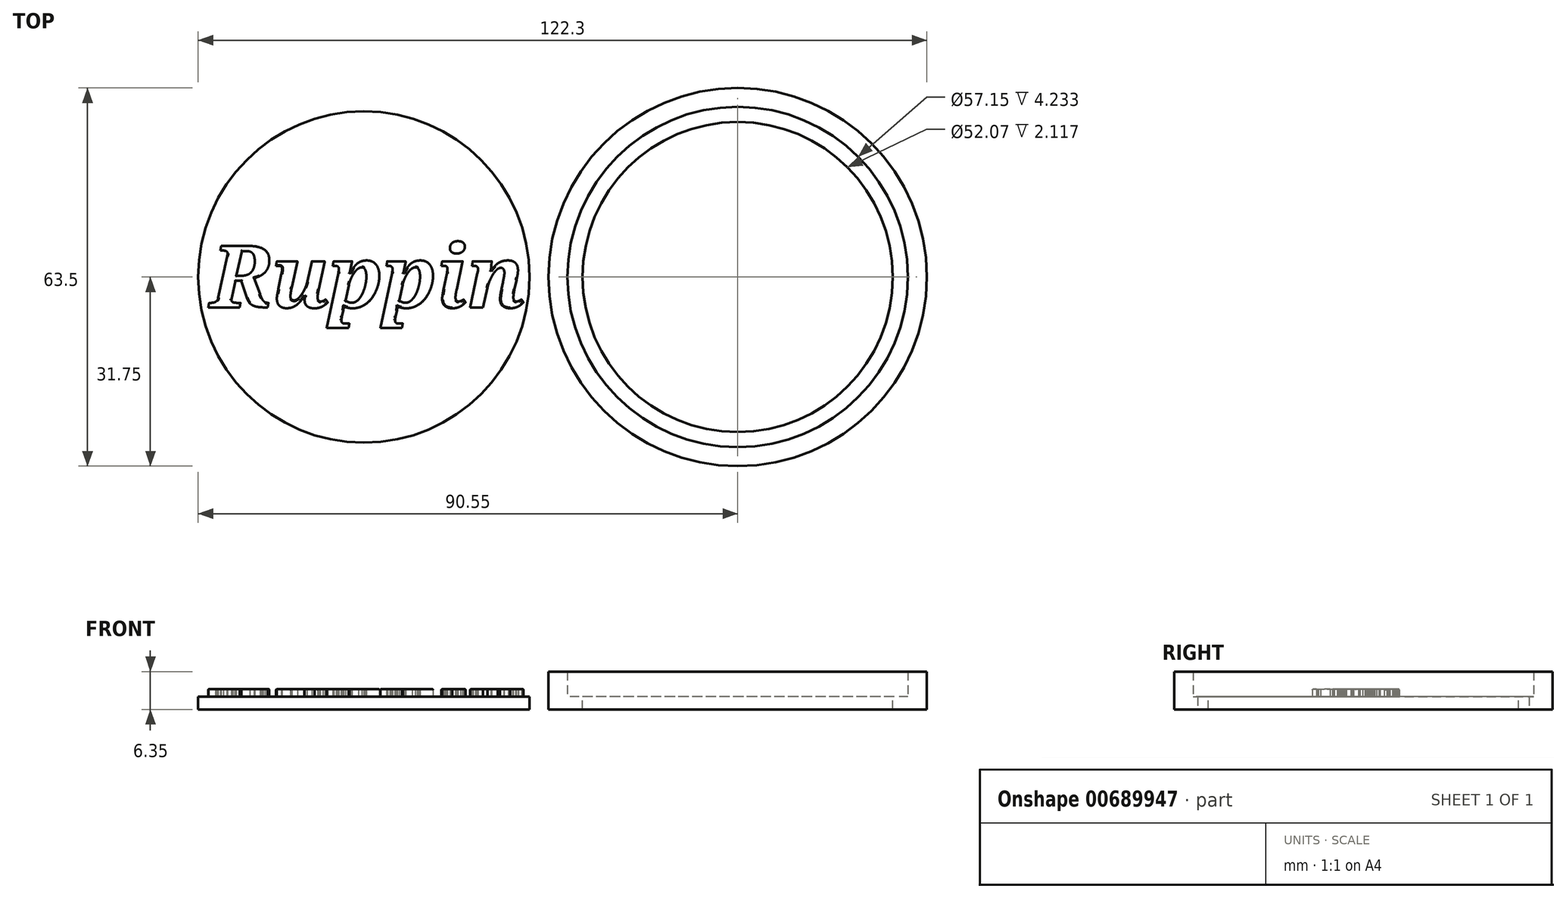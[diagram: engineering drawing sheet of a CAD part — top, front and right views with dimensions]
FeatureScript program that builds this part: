
annotation { "Feature Type Name" : "Feature", "Feature Type Description" : "" }
export const myFeature = defineFeature(function(context is Context, id is Id, definition is map)
    precondition{}
    {
        {
            var Q0;
            Q0=qCreatedBy(makeId("Top.planeOp"),FACE);
            var sketch = newSketch(context, id + "F0", { "sketchPlane" : qUnion([Q0])});
            skCircle(sketch, "E0", {"center": v(0, 0) * mm, "radius": 31.75 * mm});
            skCircle(sketch, "E1.0", {"center": v(0, 0) * mm, "radius": 28.57 * mm});
            skCircle(sketch, "E2.0", {"center": v(0, 0) * mm, "radius": 26.04 * mm});
            skCircle(sketch, "E3.0", {"center": v(0, 0) * mm, "radius": 27.81 * mm});
            skSolve(sketch);
        }
        {
            var Q0;
            Q0=makeQuery(id+"F0.imprint","IMPRINT",FACE,{"disambiguationData":[TD([[makeQuery(id+"F0.imprint","IMPRINT",EDGE,{"derivedFrom":sQuery(id+"F0.wireOp",EDGE,"E0")}),1.0]])]});
            extrude(context, id + "F1", {"entities" : qUnion([Q0]), "depth" : 2.12 * mm, "offsetDistance" : 25.4 * mm});
        }
        {
            var Q0;
            Q0=makeQuery(id+"F1.opExtrude","CAP_FACE",FACE,{"disambiguationData":[OSD([sQuery(id+"F0.wireOp",EDGE,"E0"),sQuery(id+"F0.wireOp",EDGE,"E1.0")])],"isStart":false});
            extrude(context, id + "F2", {"entities" : qUnion([Q0]), "operationType" : NewBodyOperationType.ADD, "depth" : 2.12 * mm, "offsetDistance" : 25.4 * mm});
        }
        {
            var Q0;
            Q0=makeQuery(id+"F0.imprint","IMPRINT",FACE,{"disambiguationData":[TD([[makeQuery(id+"F0.imprint","IMPRINT",EDGE,{"derivedFrom":sQuery(id+"F0.wireOp",EDGE,"E1.0")}),1.0]])]});
            var Q1;
            Q1=makeQuery(id+"F0.imprint","IMPRINT",FACE,{"disambiguationData":[TD([[makeQuery(id+"F0.imprint","IMPRINT",EDGE,{"derivedFrom":sQuery(id+"F0.wireOp",EDGE,"E0")}),1.0]])]});
            var Q2;
            Q2=makeQuery(id+"F0.imprint","IMPRINT",FACE,{"disambiguationData":[TD([[makeQuery(id+"F0.imprint","IMPRINT",EDGE,{"derivedFrom":sQuery(id+"F0.wireOp",EDGE,"E2.0")}),-1.0]])]});
            extrude(context, id + "F3", {"entities" : qUnion([Q0, Q1, Q2]), "operationType" : NewBodyOperationType.ADD, "oppositeDirection" : true, "depth" : 2.12 * mm, "offsetDistance" : 25.4 * mm});
        }
        {
            var Q0;
            Q0=makeQuery(id+"F0.imprint","IMPRINT",FACE,{"disambiguationData":[TD([[makeQuery(id+"F0.imprint","IMPRINT",EDGE,{"derivedFrom":sQuery(id+"F0.wireOp",EDGE,"E2.0")}),1.0]])]});
            var Q1;
            Q1=makeQuery(id+"F0.imprint","IMPRINT",FACE,{"disambiguationData":[TD([[makeQuery(id+"F0.imprint","IMPRINT",EDGE,{"derivedFrom":sQuery(id+"F0.wireOp",EDGE,"E2.0")}),-1.0]])]});
            extrude(context, id + "F4", {"entities" : qUnion([Q0, Q1]), "depth" : 2.12 * mm, "offsetDistance" : 25.4 * mm});
        }
        {
            var Q0;
            Q0=makeQuery(id+"F4.opExtrude","CAP_FACE",FACE,{"disambiguationData":[OSD([sQuery(id+"F0.wireOp",EDGE,"E3.0")])],"isStart":false});
            var sketch = newSketch(context, id + "F5", { "sketchPlane" : qUnion([Q0])});
            skText(sketch, "E4", { "text": "Ruppin", "fontName": "NotoSerif-BoldItalic.ttf"});
            const initialGuessF5  = {"E4": [-0.02578, -0.00511, 1, 0, 0.01041]};
            skSetInitialGuess(sketch, initialGuessF5);
            skSolve(sketch);
        }
        {
            var Q0;
            Q0 = qSketchRegion(id + "F5", true);
            extrude(context, id + "F6", {"entities" : qUnion([Q0]), "operationType" : NewBodyOperationType.ADD, "depth" : 1.27 * mm, "offsetDistance" : 25.4 * mm});
        }
        {
            var Q0;
            Q0=makeQuery(id+"F6.opExtrude","CAP_FACE",FACE,{"disambiguationData":[OSD([sQuery(id+"F5.wireOp",EDGE,"E4.sketch_text.stroke-0"),sQuery(id+"F5.wireOp",EDGE,"E4.sketch_text.stroke-1"),sQuery(id+"F5.wireOp",EDGE,"E4.sketch_text.stroke-2"),sQuery(id+"F5.wireOp",EDGE,"E4.sketch_text.stroke-3"),sQuery(id+"F5.wireOp",EDGE,"E4.sketch_text.stroke-4"),sQuery(id+"F5.wireOp",EDGE,"E4.sketch_text.stroke-5"),sQuery(id+"F5.wireOp",EDGE,"E4.sketch_text.stroke-6"),sQuery(id+"F5.wireOp",EDGE,"E4.sketch_text.stroke-7"),sQuery(id+"F5.wireOp",EDGE,"E4.sketch_text.stroke-8"),sQuery(id+"F5.wireOp",EDGE,"E4.sketch_text.stroke-9"),sQuery(id+"F5.wireOp",EDGE,"E4.sketch_text.stroke-10"),sQuery(id+"F5.wireOp",EDGE,"E4.sketch_text.stroke-11"),sQuery(id+"F5.wireOp",EDGE,"E4.sketch_text.stroke-12"),sQuery(id+"F5.wireOp",EDGE,"E4.sketch_text.stroke-13"),sQuery(id+"F5.wireOp",EDGE,"E4.sketch_text.stroke-14"),sQuery(id+"F5.wireOp",EDGE,"E4.sketch_text.stroke-15"),sQuery(id+"F5.wireOp",EDGE,"E4.sketch_text.stroke-16"),sQuery(id+"F5.wireOp",EDGE,"E4.sketch_text.stroke-17"),sQuery(id+"F5.wireOp",EDGE,"E4.sketch_text.stroke-18"),sQuery(id+"F5.wireOp",EDGE,"E4.sketch_text.stroke-19"),sQuery(id+"F5.wireOp",EDGE,"E4.sketch_text.stroke-20"),sQuery(id+"F5.wireOp",EDGE,"E4.sketch_text.stroke-21"),sQuery(id+"F5.wireOp",EDGE,"E4.sketch_text.stroke-22"),sQuery(id+"F5.wireOp",EDGE,"E4.sketch_text.stroke-23"),sQuery(id+"F5.wireOp",EDGE,"E4.sketch_text.stroke-24"),sQuery(id+"F5.wireOp",EDGE,"E4.sketch_text.stroke-25"),sQuery(id+"F5.wireOp",EDGE,"E4.sketch_text.stroke-26"),sQuery(id+"F5.wireOp",EDGE,"E4.sketch_text.stroke-27"),sQuery(id+"F5.wireOp",EDGE,"E4.sketch_text.stroke-28"),sQuery(id+"F5.wireOp",EDGE,"E4.sketch_text.stroke-29"),sQuery(id+"F5.wireOp",EDGE,"E4.sketch_text.stroke-30"),sQuery(id+"F5.wireOp",EDGE,"E4.sketch_text.stroke-31"),sQuery(id+"F5.wireOp",EDGE,"E4.sketch_text.stroke-32"),sQuery(id+"F5.wireOp",EDGE,"E4.sketch_text.stroke-33"),sQuery(id+"F5.wireOp",EDGE,"E4.sketch_text.stroke-34"),sQuery(id+"F5.wireOp",EDGE,"E4.sketch_text.stroke-35"),sQuery(id+"F5.wireOp",EDGE,"E4.sketch_text.stroke-36"),sQuery(id+"F5.wireOp",EDGE,"E4.sketch_text.stroke-37"),sQuery(id+"F5.wireOp",EDGE,"E4.sketch_text.stroke-38"),sQuery(id+"F5.wireOp",EDGE,"E4.sketch_text.stroke-39"),sQuery(id+"F5.wireOp",EDGE,"E4.sketch_text.stroke-40"),sQuery(id+"F5.wireOp",EDGE,"E4.sketch_text.stroke-41"),sQuery(id+"F5.wireOp",EDGE,"E4.sketch_text.stroke-42"),sQuery(id+"F5.wireOp",EDGE,"E4.sketch_text.stroke-43"),sQuery(id+"F5.wireOp",EDGE,"E4.sketch_text.stroke-44"),sQuery(id+"F5.wireOp",EDGE,"E4.sketch_text.stroke-45"),sQuery(id+"F5.wireOp",EDGE,"E4.sketch_text.stroke-46"),sQuery(id+"F5.wireOp",EDGE,"E4.sketch_text.stroke-47"),sQuery(id+"F5.wireOp",EDGE,"E4.sketch_text.stroke-48"),sQuery(id+"F5.wireOp",EDGE,"E4.sketch_text.stroke-49"),sQuery(id+"F5.wireOp",EDGE,"E4.sketch_text.stroke-50"),sQuery(id+"F5.wireOp",EDGE,"E4.sketch_text.stroke-51"),sQuery(id+"F5.wireOp",EDGE,"E4.sketch_text.stroke-52"),sQuery(id+"F5.wireOp",EDGE,"E4.sketch_text.stroke-53"),sQuery(id+"F5.wireOp",EDGE,"E4.sketch_text.stroke-54"),sQuery(id+"F5.wireOp",EDGE,"E4.sketch_text.stroke-55")])],"isStart":false});
            var Q1;
            Q1=makeQuery(id+"F6.opExtrude","CAP_FACE",FACE,{"disambiguationData":[OSD([sQuery(id+"F5.wireOp",EDGE,"E4.sketch_text.stroke-56"),sQuery(id+"F5.wireOp",EDGE,"E4.sketch_text.stroke-57"),sQuery(id+"F5.wireOp",EDGE,"E4.sketch_text.stroke-58"),sQuery(id+"F5.wireOp",EDGE,"E4.sketch_text.stroke-59"),sQuery(id+"F5.wireOp",EDGE,"E4.sketch_text.stroke-60"),sQuery(id+"F5.wireOp",EDGE,"E4.sketch_text.stroke-61"),sQuery(id+"F5.wireOp",EDGE,"E4.sketch_text.stroke-62"),sQuery(id+"F5.wireOp",EDGE,"E4.sketch_text.stroke-63"),sQuery(id+"F5.wireOp",EDGE,"E4.sketch_text.stroke-64"),sQuery(id+"F5.wireOp",EDGE,"E4.sketch_text.stroke-65"),sQuery(id+"F5.wireOp",EDGE,"E4.sketch_text.stroke-66"),sQuery(id+"F5.wireOp",EDGE,"E4.sketch_text.stroke-67"),sQuery(id+"F5.wireOp",EDGE,"E4.sketch_text.stroke-68"),sQuery(id+"F5.wireOp",EDGE,"E4.sketch_text.stroke-69"),sQuery(id+"F5.wireOp",EDGE,"E4.sketch_text.stroke-70"),sQuery(id+"F5.wireOp",EDGE,"E4.sketch_text.stroke-71"),sQuery(id+"F5.wireOp",EDGE,"E4.sketch_text.stroke-72"),sQuery(id+"F5.wireOp",EDGE,"E4.sketch_text.stroke-73"),sQuery(id+"F5.wireOp",EDGE,"E4.sketch_text.stroke-74"),sQuery(id+"F5.wireOp",EDGE,"E4.sketch_text.stroke-75"),sQuery(id+"F5.wireOp",EDGE,"E4.sketch_text.stroke-76"),sQuery(id+"F5.wireOp",EDGE,"E4.sketch_text.stroke-77"),sQuery(id+"F5.wireOp",EDGE,"E4.sketch_text.stroke-78"),sQuery(id+"F5.wireOp",EDGE,"E4.sketch_text.stroke-79"),sQuery(id+"F5.wireOp",EDGE,"E4.sketch_text.stroke-80"),sQuery(id+"F5.wireOp",EDGE,"E4.sketch_text.stroke-81"),sQuery(id+"F5.wireOp",EDGE,"E4.sketch_text.stroke-82"),sQuery(id+"F5.wireOp",EDGE,"E4.sketch_text.stroke-83"),sQuery(id+"F5.wireOp",EDGE,"E4.sketch_text.stroke-84"),sQuery(id+"F5.wireOp",EDGE,"E4.sketch_text.stroke-85"),sQuery(id+"F5.wireOp",EDGE,"E4.sketch_text.stroke-86"),sQuery(id+"F5.wireOp",EDGE,"E4.sketch_text.stroke-87"),sQuery(id+"F5.wireOp",EDGE,"E4.sketch_text.stroke-88"),sQuery(id+"F5.wireOp",EDGE,"E4.sketch_text.stroke-89"),sQuery(id+"F5.wireOp",EDGE,"E4.sketch_text.stroke-90"),sQuery(id+"F5.wireOp",EDGE,"E4.sketch_text.stroke-91"),sQuery(id+"F5.wireOp",EDGE,"E4.sketch_text.stroke-92"),sQuery(id+"F5.wireOp",EDGE,"E4.sketch_text.stroke-93"),sQuery(id+"F5.wireOp",EDGE,"E4.sketch_text.stroke-94"),sQuery(id+"F5.wireOp",EDGE,"E4.sketch_text.stroke-95"),sQuery(id+"F5.wireOp",EDGE,"E4.sketch_text.stroke-96"),sQuery(id+"F5.wireOp",EDGE,"E4.sketch_text.stroke-97"),sQuery(id+"F5.wireOp",EDGE,"E4.sketch_text.stroke-98"),sQuery(id+"F5.wireOp",EDGE,"E4.sketch_text.stroke-99"),sQuery(id+"F5.wireOp",EDGE,"E4.sketch_text.stroke-100"),sQuery(id+"F5.wireOp",EDGE,"E4.sketch_text.stroke-101"),sQuery(id+"F5.wireOp",EDGE,"E4.sketch_text.stroke-102"),sQuery(id+"F5.wireOp",EDGE,"E4.sketch_text.stroke-103"),sQuery(id+"F5.wireOp",EDGE,"E4.sketch_text.stroke-104"),sQuery(id+"F5.wireOp",EDGE,"E4.sketch_text.stroke-105"),sQuery(id+"F5.wireOp",EDGE,"E4.sketch_text.stroke-106"),sQuery(id+"F5.wireOp",EDGE,"E4.sketch_text.stroke-107")])],"isStart":false});
            var Q2;
            Q2=makeQuery(id+"F6.opExtrude","CAP_FACE",FACE,{"disambiguationData":[OSD([sQuery(id+"F5.wireOp",EDGE,"E4.sketch_text.stroke-108"),sQuery(id+"F5.wireOp",EDGE,"E4.sketch_text.stroke-109"),sQuery(id+"F5.wireOp",EDGE,"E4.sketch_text.stroke-110"),sQuery(id+"F5.wireOp",EDGE,"E4.sketch_text.stroke-111"),sQuery(id+"F5.wireOp",EDGE,"E4.sketch_text.stroke-112"),sQuery(id+"F5.wireOp",EDGE,"E4.sketch_text.stroke-113"),sQuery(id+"F5.wireOp",EDGE,"E4.sketch_text.stroke-114"),sQuery(id+"F5.wireOp",EDGE,"E4.sketch_text.stroke-115"),sQuery(id+"F5.wireOp",EDGE,"E4.sketch_text.stroke-116"),sQuery(id+"F5.wireOp",EDGE,"E4.sketch_text.stroke-117"),sQuery(id+"F5.wireOp",EDGE,"E4.sketch_text.stroke-118"),sQuery(id+"F5.wireOp",EDGE,"E4.sketch_text.stroke-119"),sQuery(id+"F5.wireOp",EDGE,"E4.sketch_text.stroke-120"),sQuery(id+"F5.wireOp",EDGE,"E4.sketch_text.stroke-121"),sQuery(id+"F5.wireOp",EDGE,"E4.sketch_text.stroke-122"),sQuery(id+"F5.wireOp",EDGE,"E4.sketch_text.stroke-123"),sQuery(id+"F5.wireOp",EDGE,"E4.sketch_text.stroke-124"),sQuery(id+"F5.wireOp",EDGE,"E4.sketch_text.stroke-125"),sQuery(id+"F5.wireOp",EDGE,"E4.sketch_text.stroke-126"),sQuery(id+"F5.wireOp",EDGE,"E4.sketch_text.stroke-127"),sQuery(id+"F5.wireOp",EDGE,"E4.sketch_text.stroke-128"),sQuery(id+"F5.wireOp",EDGE,"E4.sketch_text.stroke-129"),sQuery(id+"F5.wireOp",EDGE,"E4.sketch_text.stroke-130"),sQuery(id+"F5.wireOp",EDGE,"E4.sketch_text.stroke-131"),sQuery(id+"F5.wireOp",EDGE,"E4.sketch_text.stroke-132"),sQuery(id+"F5.wireOp",EDGE,"E4.sketch_text.stroke-133"),sQuery(id+"F5.wireOp",EDGE,"E4.sketch_text.stroke-134"),sQuery(id+"F5.wireOp",EDGE,"E4.sketch_text.stroke-135"),sQuery(id+"F5.wireOp",EDGE,"E4.sketch_text.stroke-136"),sQuery(id+"F5.wireOp",EDGE,"E4.sketch_text.stroke-137"),sQuery(id+"F5.wireOp",EDGE,"E4.sketch_text.stroke-138"),sQuery(id+"F5.wireOp",EDGE,"E4.sketch_text.stroke-139"),sQuery(id+"F5.wireOp",EDGE,"E4.sketch_text.stroke-140"),sQuery(id+"F5.wireOp",EDGE,"E4.sketch_text.stroke-141"),sQuery(id+"F5.wireOp",EDGE,"E4.sketch_text.stroke-142"),sQuery(id+"F5.wireOp",EDGE,"E4.sketch_text.stroke-143"),sQuery(id+"F5.wireOp",EDGE,"E4.sketch_text.stroke-144"),sQuery(id+"F5.wireOp",EDGE,"E4.sketch_text.stroke-145"),sQuery(id+"F5.wireOp",EDGE,"E4.sketch_text.stroke-146"),sQuery(id+"F5.wireOp",EDGE,"E4.sketch_text.stroke-147"),sQuery(id+"F5.wireOp",EDGE,"E4.sketch_text.stroke-148"),sQuery(id+"F5.wireOp",EDGE,"E4.sketch_text.stroke-149"),sQuery(id+"F5.wireOp",EDGE,"E4.sketch_text.stroke-150"),sQuery(id+"F5.wireOp",EDGE,"E4.sketch_text.stroke-151"),sQuery(id+"F5.wireOp",EDGE,"E4.sketch_text.stroke-152"),sQuery(id+"F5.wireOp",EDGE,"E4.sketch_text.stroke-153"),sQuery(id+"F5.wireOp",EDGE,"E4.sketch_text.stroke-154"),sQuery(id+"F5.wireOp",EDGE,"E4.sketch_text.stroke-155"),sQuery(id+"F5.wireOp",EDGE,"E4.sketch_text.stroke-156"),sQuery(id+"F5.wireOp",EDGE,"E4.sketch_text.stroke-157"),sQuery(id+"F5.wireOp",EDGE,"E4.sketch_text.stroke-158"),sQuery(id+"F5.wireOp",EDGE,"E4.sketch_text.stroke-159"),sQuery(id+"F5.wireOp",EDGE,"E4.sketch_text.stroke-160"),sQuery(id+"F5.wireOp",EDGE,"E4.sketch_text.stroke-161"),sQuery(id+"F5.wireOp",EDGE,"E4.sketch_text.stroke-162"),sQuery(id+"F5.wireOp",EDGE,"E4.sketch_text.stroke-163"),sQuery(id+"F5.wireOp",EDGE,"E4.sketch_text.stroke-164"),sQuery(id+"F5.wireOp",EDGE,"E4.sketch_text.stroke-165"),sQuery(id+"F5.wireOp",EDGE,"E4.sketch_text.stroke-166"),sQuery(id+"F5.wireOp",EDGE,"E4.sketch_text.stroke-167"),sQuery(id+"F5.wireOp",EDGE,"E4.sketch_text.stroke-168"),sQuery(id+"F5.wireOp",EDGE,"E4.sketch_text.stroke-169"),sQuery(id+"F5.wireOp",EDGE,"E4.sketch_text.stroke-170"),sQuery(id+"F5.wireOp",EDGE,"E4.sketch_text.stroke-171"),sQuery(id+"F5.wireOp",EDGE,"E4.sketch_text.stroke-172"),sQuery(id+"F5.wireOp",EDGE,"E4.sketch_text.stroke-173")])],"isStart":false});
            var Q3;
            Q3=makeQuery(id+"F6.opExtrude","CAP_FACE",FACE,{"disambiguationData":[OSD([sQuery(id+"F5.wireOp",EDGE,"E4.sketch_text.stroke-174"),sQuery(id+"F5.wireOp",EDGE,"E4.sketch_text.stroke-175"),sQuery(id+"F5.wireOp",EDGE,"E4.sketch_text.stroke-176"),sQuery(id+"F5.wireOp",EDGE,"E4.sketch_text.stroke-177"),sQuery(id+"F5.wireOp",EDGE,"E4.sketch_text.stroke-178"),sQuery(id+"F5.wireOp",EDGE,"E4.sketch_text.stroke-179"),sQuery(id+"F5.wireOp",EDGE,"E4.sketch_text.stroke-180"),sQuery(id+"F5.wireOp",EDGE,"E4.sketch_text.stroke-181"),sQuery(id+"F5.wireOp",EDGE,"E4.sketch_text.stroke-182"),sQuery(id+"F5.wireOp",EDGE,"E4.sketch_text.stroke-183"),sQuery(id+"F5.wireOp",EDGE,"E4.sketch_text.stroke-184"),sQuery(id+"F5.wireOp",EDGE,"E4.sketch_text.stroke-185"),sQuery(id+"F5.wireOp",EDGE,"E4.sketch_text.stroke-186"),sQuery(id+"F5.wireOp",EDGE,"E4.sketch_text.stroke-187"),sQuery(id+"F5.wireOp",EDGE,"E4.sketch_text.stroke-188"),sQuery(id+"F5.wireOp",EDGE,"E4.sketch_text.stroke-189"),sQuery(id+"F5.wireOp",EDGE,"E4.sketch_text.stroke-190"),sQuery(id+"F5.wireOp",EDGE,"E4.sketch_text.stroke-191"),sQuery(id+"F5.wireOp",EDGE,"E4.sketch_text.stroke-192"),sQuery(id+"F5.wireOp",EDGE,"E4.sketch_text.stroke-193"),sQuery(id+"F5.wireOp",EDGE,"E4.sketch_text.stroke-194"),sQuery(id+"F5.wireOp",EDGE,"E4.sketch_text.stroke-195"),sQuery(id+"F5.wireOp",EDGE,"E4.sketch_text.stroke-196"),sQuery(id+"F5.wireOp",EDGE,"E4.sketch_text.stroke-197"),sQuery(id+"F5.wireOp",EDGE,"E4.sketch_text.stroke-198"),sQuery(id+"F5.wireOp",EDGE,"E4.sketch_text.stroke-199"),sQuery(id+"F5.wireOp",EDGE,"E4.sketch_text.stroke-200"),sQuery(id+"F5.wireOp",EDGE,"E4.sketch_text.stroke-201"),sQuery(id+"F5.wireOp",EDGE,"E4.sketch_text.stroke-202"),sQuery(id+"F5.wireOp",EDGE,"E4.sketch_text.stroke-203"),sQuery(id+"F5.wireOp",EDGE,"E4.sketch_text.stroke-204"),sQuery(id+"F5.wireOp",EDGE,"E4.sketch_text.stroke-205"),sQuery(id+"F5.wireOp",EDGE,"E4.sketch_text.stroke-206"),sQuery(id+"F5.wireOp",EDGE,"E4.sketch_text.stroke-207"),sQuery(id+"F5.wireOp",EDGE,"E4.sketch_text.stroke-208"),sQuery(id+"F5.wireOp",EDGE,"E4.sketch_text.stroke-209"),sQuery(id+"F5.wireOp",EDGE,"E4.sketch_text.stroke-210"),sQuery(id+"F5.wireOp",EDGE,"E4.sketch_text.stroke-211"),sQuery(id+"F5.wireOp",EDGE,"E4.sketch_text.stroke-212"),sQuery(id+"F5.wireOp",EDGE,"E4.sketch_text.stroke-213"),sQuery(id+"F5.wireOp",EDGE,"E4.sketch_text.stroke-214"),sQuery(id+"F5.wireOp",EDGE,"E4.sketch_text.stroke-215"),sQuery(id+"F5.wireOp",EDGE,"E4.sketch_text.stroke-216"),sQuery(id+"F5.wireOp",EDGE,"E4.sketch_text.stroke-217"),sQuery(id+"F5.wireOp",EDGE,"E4.sketch_text.stroke-218"),sQuery(id+"F5.wireOp",EDGE,"E4.sketch_text.stroke-219"),sQuery(id+"F5.wireOp",EDGE,"E4.sketch_text.stroke-220"),sQuery(id+"F5.wireOp",EDGE,"E4.sketch_text.stroke-221"),sQuery(id+"F5.wireOp",EDGE,"E4.sketch_text.stroke-222"),sQuery(id+"F5.wireOp",EDGE,"E4.sketch_text.stroke-223"),sQuery(id+"F5.wireOp",EDGE,"E4.sketch_text.stroke-224"),sQuery(id+"F5.wireOp",EDGE,"E4.sketch_text.stroke-225"),sQuery(id+"F5.wireOp",EDGE,"E4.sketch_text.stroke-226"),sQuery(id+"F5.wireOp",EDGE,"E4.sketch_text.stroke-227"),sQuery(id+"F5.wireOp",EDGE,"E4.sketch_text.stroke-228"),sQuery(id+"F5.wireOp",EDGE,"E4.sketch_text.stroke-229"),sQuery(id+"F5.wireOp",EDGE,"E4.sketch_text.stroke-230"),sQuery(id+"F5.wireOp",EDGE,"E4.sketch_text.stroke-231"),sQuery(id+"F5.wireOp",EDGE,"E4.sketch_text.stroke-232"),sQuery(id+"F5.wireOp",EDGE,"E4.sketch_text.stroke-233"),sQuery(id+"F5.wireOp",EDGE,"E4.sketch_text.stroke-234"),sQuery(id+"F5.wireOp",EDGE,"E4.sketch_text.stroke-235"),sQuery(id+"F5.wireOp",EDGE,"E4.sketch_text.stroke-236"),sQuery(id+"F5.wireOp",EDGE,"E4.sketch_text.stroke-237"),sQuery(id+"F5.wireOp",EDGE,"E4.sketch_text.stroke-238"),sQuery(id+"F5.wireOp",EDGE,"E4.sketch_text.stroke-239")])],"isStart":false});
            var Q4;
            Q4=makeQuery(id+"F6.opExtrude","CAP_FACE",FACE,{"disambiguationData":[OSD([sQuery(id+"F5.wireOp",EDGE,"E4.sketch_text.stroke-240"),sQuery(id+"F5.wireOp",EDGE,"E4.sketch_text.stroke-241"),sQuery(id+"F5.wireOp",EDGE,"E4.sketch_text.stroke-242"),sQuery(id+"F5.wireOp",EDGE,"E4.sketch_text.stroke-243"),sQuery(id+"F5.wireOp",EDGE,"E4.sketch_text.stroke-244"),sQuery(id+"F5.wireOp",EDGE,"E4.sketch_text.stroke-245"),sQuery(id+"F5.wireOp",EDGE,"E4.sketch_text.stroke-246"),sQuery(id+"F5.wireOp",EDGE,"E4.sketch_text.stroke-247"),sQuery(id+"F5.wireOp",EDGE,"E4.sketch_text.stroke-248"),sQuery(id+"F5.wireOp",EDGE,"E4.sketch_text.stroke-249"),sQuery(id+"F5.wireOp",EDGE,"E4.sketch_text.stroke-250"),sQuery(id+"F5.wireOp",EDGE,"E4.sketch_text.stroke-251"),sQuery(id+"F5.wireOp",EDGE,"E4.sketch_text.stroke-252"),sQuery(id+"F5.wireOp",EDGE,"E4.sketch_text.stroke-253"),sQuery(id+"F5.wireOp",EDGE,"E4.sketch_text.stroke-254"),sQuery(id+"F5.wireOp",EDGE,"E4.sketch_text.stroke-255"),sQuery(id+"F5.wireOp",EDGE,"E4.sketch_text.stroke-256"),sQuery(id+"F5.wireOp",EDGE,"E4.sketch_text.stroke-257"),sQuery(id+"F5.wireOp",EDGE,"E4.sketch_text.stroke-258"),sQuery(id+"F5.wireOp",EDGE,"E4.sketch_text.stroke-259"),sQuery(id+"F5.wireOp",EDGE,"E4.sketch_text.stroke-260"),sQuery(id+"F5.wireOp",EDGE,"E4.sketch_text.stroke-261"),sQuery(id+"F5.wireOp",EDGE,"E4.sketch_text.stroke-262"),sQuery(id+"F5.wireOp",EDGE,"E4.sketch_text.stroke-263"),sQuery(id+"F5.wireOp",EDGE,"E4.sketch_text.stroke-264"),sQuery(id+"F5.wireOp",EDGE,"E4.sketch_text.stroke-265"),sQuery(id+"F5.wireOp",EDGE,"E4.sketch_text.stroke-266"),sQuery(id+"F5.wireOp",EDGE,"E4.sketch_text.stroke-267")])],"isStart":false});
            var Q5;
            Q5=makeQuery(id+"F6.opExtrude","CAP_FACE",FACE,{"disambiguationData":[OSD([sQuery(id+"F5.wireOp",EDGE,"E4.sketch_text.stroke-284"),sQuery(id+"F5.wireOp",EDGE,"E4.sketch_text.stroke-285"),sQuery(id+"F5.wireOp",EDGE,"E4.sketch_text.stroke-286"),sQuery(id+"F5.wireOp",EDGE,"E4.sketch_text.stroke-287"),sQuery(id+"F5.wireOp",EDGE,"E4.sketch_text.stroke-288"),sQuery(id+"F5.wireOp",EDGE,"E4.sketch_text.stroke-289"),sQuery(id+"F5.wireOp",EDGE,"E4.sketch_text.stroke-290"),sQuery(id+"F5.wireOp",EDGE,"E4.sketch_text.stroke-291"),sQuery(id+"F5.wireOp",EDGE,"E4.sketch_text.stroke-292"),sQuery(id+"F5.wireOp",EDGE,"E4.sketch_text.stroke-293"),sQuery(id+"F5.wireOp",EDGE,"E4.sketch_text.stroke-294"),sQuery(id+"F5.wireOp",EDGE,"E4.sketch_text.stroke-295"),sQuery(id+"F5.wireOp",EDGE,"E4.sketch_text.stroke-296"),sQuery(id+"F5.wireOp",EDGE,"E4.sketch_text.stroke-297"),sQuery(id+"F5.wireOp",EDGE,"E4.sketch_text.stroke-298"),sQuery(id+"F5.wireOp",EDGE,"E4.sketch_text.stroke-299"),sQuery(id+"F5.wireOp",EDGE,"E4.sketch_text.stroke-300"),sQuery(id+"F5.wireOp",EDGE,"E4.sketch_text.stroke-301"),sQuery(id+"F5.wireOp",EDGE,"E4.sketch_text.stroke-302"),sQuery(id+"F5.wireOp",EDGE,"E4.sketch_text.stroke-303"),sQuery(id+"F5.wireOp",EDGE,"E4.sketch_text.stroke-304"),sQuery(id+"F5.wireOp",EDGE,"E4.sketch_text.stroke-305"),sQuery(id+"F5.wireOp",EDGE,"E4.sketch_text.stroke-306"),sQuery(id+"F5.wireOp",EDGE,"E4.sketch_text.stroke-307"),sQuery(id+"F5.wireOp",EDGE,"E4.sketch_text.stroke-308"),sQuery(id+"F5.wireOp",EDGE,"E4.sketch_text.stroke-309"),sQuery(id+"F5.wireOp",EDGE,"E4.sketch_text.stroke-310"),sQuery(id+"F5.wireOp",EDGE,"E4.sketch_text.stroke-311"),sQuery(id+"F5.wireOp",EDGE,"E4.sketch_text.stroke-312"),sQuery(id+"F5.wireOp",EDGE,"E4.sketch_text.stroke-313"),sQuery(id+"F5.wireOp",EDGE,"E4.sketch_text.stroke-314"),sQuery(id+"F5.wireOp",EDGE,"E4.sketch_text.stroke-315"),sQuery(id+"F5.wireOp",EDGE,"E4.sketch_text.stroke-316"),sQuery(id+"F5.wireOp",EDGE,"E4.sketch_text.stroke-317"),sQuery(id+"F5.wireOp",EDGE,"E4.sketch_text.stroke-318"),sQuery(id+"F5.wireOp",EDGE,"E4.sketch_text.stroke-319"),sQuery(id+"F5.wireOp",EDGE,"E4.sketch_text.stroke-320"),sQuery(id+"F5.wireOp",EDGE,"E4.sketch_text.stroke-321"),sQuery(id+"F5.wireOp",EDGE,"E4.sketch_text.stroke-322"),sQuery(id+"F5.wireOp",EDGE,"E4.sketch_text.stroke-323"),sQuery(id+"F5.wireOp",EDGE,"E4.sketch_text.stroke-324"),sQuery(id+"F5.wireOp",EDGE,"E4.sketch_text.stroke-325"),sQuery(id+"F5.wireOp",EDGE,"E4.sketch_text.stroke-326"),sQuery(id+"F5.wireOp",EDGE,"E4.sketch_text.stroke-327"),sQuery(id+"F5.wireOp",EDGE,"E4.sketch_text.stroke-328"),sQuery(id+"F5.wireOp",EDGE,"E4.sketch_text.stroke-329"),sQuery(id+"F5.wireOp",EDGE,"E4.sketch_text.stroke-330"),sQuery(id+"F5.wireOp",EDGE,"E4.sketch_text.stroke-331"),sQuery(id+"F5.wireOp",EDGE,"E4.sketch_text.stroke-332"),sQuery(id+"F5.wireOp",EDGE,"E4.sketch_text.stroke-333"),sQuery(id+"F5.wireOp",EDGE,"E4.sketch_text.stroke-334"),sQuery(id+"F5.wireOp",EDGE,"E4.sketch_text.stroke-335"),sQuery(id+"F5.wireOp",EDGE,"E4.sketch_text.stroke-336"),sQuery(id+"F5.wireOp",EDGE,"E4.sketch_text.stroke-337"),sQuery(id+"F5.wireOp",EDGE,"E4.sketch_text.stroke-338"),sQuery(id+"F5.wireOp",EDGE,"E4.sketch_text.stroke-339"),sQuery(id+"F5.wireOp",EDGE,"E4.sketch_text.stroke-340"),sQuery(id+"F5.wireOp",EDGE,"E4.sketch_text.stroke-341")])],"isStart":false});
            var Q6;
            Q6=makeQuery(id+"F6.opExtrude","CAP_FACE",FACE,{"disambiguationData":[OSD([sQuery(id+"F5.wireOp",EDGE,"E4.sketch_text.stroke-268"),sQuery(id+"F5.wireOp",EDGE,"E4.sketch_text.stroke-269"),sQuery(id+"F5.wireOp",EDGE,"E4.sketch_text.stroke-270"),sQuery(id+"F5.wireOp",EDGE,"E4.sketch_text.stroke-271"),sQuery(id+"F5.wireOp",EDGE,"E4.sketch_text.stroke-272"),sQuery(id+"F5.wireOp",EDGE,"E4.sketch_text.stroke-273"),sQuery(id+"F5.wireOp",EDGE,"E4.sketch_text.stroke-274"),sQuery(id+"F5.wireOp",EDGE,"E4.sketch_text.stroke-275"),sQuery(id+"F5.wireOp",EDGE,"E4.sketch_text.stroke-276"),sQuery(id+"F5.wireOp",EDGE,"E4.sketch_text.stroke-277"),sQuery(id+"F5.wireOp",EDGE,"E4.sketch_text.stroke-278"),sQuery(id+"F5.wireOp",EDGE,"E4.sketch_text.stroke-279"),sQuery(id+"F5.wireOp",EDGE,"E4.sketch_text.stroke-280"),sQuery(id+"F5.wireOp",EDGE,"E4.sketch_text.stroke-281"),sQuery(id+"F5.wireOp",EDGE,"E4.sketch_text.stroke-282"),sQuery(id+"F5.wireOp",EDGE,"E4.sketch_text.stroke-283")])],"isStart":false});
            fillet(context, id + "F7", {"entities" : qUnion([Q0, Q1, Q2, Q3, Q4, Q5, Q6]), "radius" : 0.13 * mm, "tangentPropagation" : true, "allowEdgeOverflow" : false});
        }
        {
            var Q0;
            Q0=makeQuery(id+"F4.opExtrude","SWEPT_BODY",BODY,{"disambiguationData":[OSD([sQuery(id+"F0.wireOp",EDGE,"E3.0")])]});
            transform(context, id + "F8", {"entities" : qUnion([Q0]), "transformType" : TransformType.TRANSLATION_3D, "dx" : -62.74 * mm, "dy" : 0 * mm, "dz" : 0 * mm, "makeCopy" : false});
        }
        {
            var Q0;
            Q0=makeQuery(id+"F1.opExtrude","SWEPT_BODY",BODY,{"disambiguationData":[OSD([sQuery(id+"F0.wireOp",EDGE,"E0"),sQuery(id+"F0.wireOp",EDGE,"E1.0")])]});
            transform(context, id + "F9", {"entities" : qUnion([Q0]), "transformType" : TransformType.TRANSLATION_3D, "dx" : 0 * mm, "dy" : 0 * mm, "dz" : 2.12 * mm, "makeCopy" : false});
        }
    });
